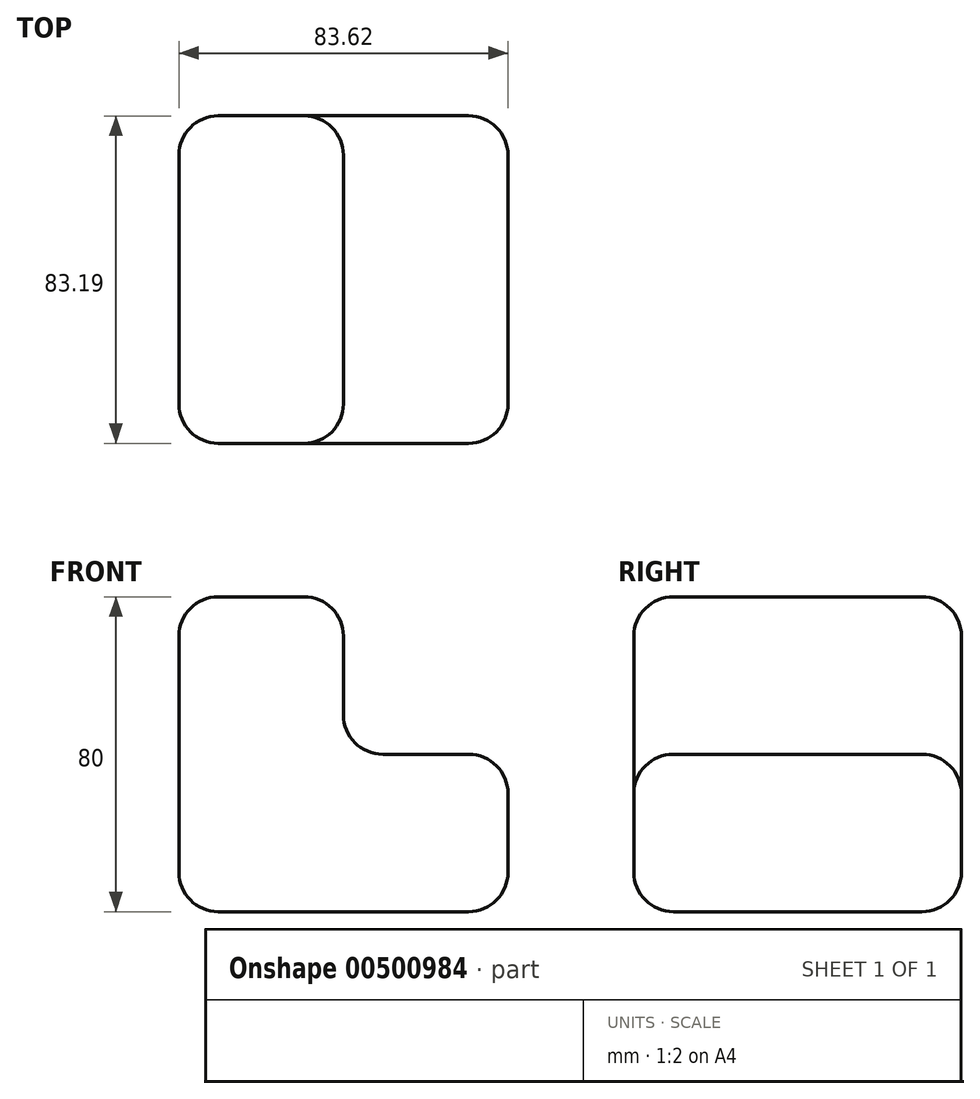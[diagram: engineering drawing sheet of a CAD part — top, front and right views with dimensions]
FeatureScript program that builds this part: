
annotation { "Feature Type Name" : "Feature", "Feature Type Description" : "" }
export const myFeature = defineFeature(function(context is Context, id is Id, definition is map)
    precondition{}
    {
        {
            var Q0;
            Q0=qCreatedBy(makeId("Top.planeOp"),FACE);
            var sketch = newSketch(context, id + "F0", { "sketchPlane" : qUnion([Q0])});
            skLineSegment(sketch, "E0.bottom", {"start": v(-59.13, -45.93) * mm, "end": v(24.5, -45.93) * mm});
            skLineSegment(sketch, "E0.top", {"start": v(-59.13, 37.26) * mm, "end": v(24.5, 37.26) * mm});
            skLineSegment(sketch, "E0.left", {"start": v(-59.13, -45.93) * mm, "end": v(-59.13, 37.26) * mm});
            skLineSegment(sketch, "E0.right", {"start": v(24.5, -45.93) * mm, "end": v(24.5, 37.26) * mm});
            skSolve(sketch);
        }
        {
            var Q0;
            Q0=makeQuery(id+"F0.imprint","IMPRINT",FACE,{"disambiguationData":[TD([[makeQuery(id+"F0.imprint","IMPRINT",EDGE,{"derivedFrom":sQuery(id+"F0.wireOp",EDGE,"E0.bottom")}),1.0]])]});
            extrude(context, id + "F1", {"entities" : qUnion([Q0]), "depth" : 40 * mm});
        }
        {
            var Q0;
            Q0=makeQuery(id+"F1.opExtrude","CAP_FACE",FACE,{"disambiguationData":[OSD([sQuery(id+"F0.wireOp",EDGE,"E0.bottom"),sQuery(id+"F0.wireOp",EDGE,"E0.top"),sQuery(id+"F0.wireOp",EDGE,"E0.left"),sQuery(id+"F0.wireOp",EDGE,"E0.right")])],"isStart":false});
            var sketch = newSketch(context, id + "F2", { "sketchPlane" : qUnion([Q0])});
            skLineSegment(sketch, "E1", {"start": v(-17.32, 37.26) * mm, "end": v(-17.32, -45.93) * mm});
            skSolve(sketch);
        }
        {
            var Q0;
            {var subQ1=sQuery(id+"F2.wireOp",EDGE,"E1");Q0=makeQuery(id+"F2.imprint","IMPRINT",FACE,{"disambiguationData":[TD([[makeQuery(id+"F2.imprint","IMPRINT",EDGE,{"derivedFrom":subQ1}),-1.0]])]});}
            extrude(context, id + "F3", {"entities" : qUnion([Q0]), "operationType" : NewBodyOperationType.ADD, "depth" : 40 * mm});
        }
        {
            var Q0;
            Q0=makeQuery(id+"F3.opExtrude","CAP_FACE",FACE,{"disambiguationData":[OSD([sQuery(id+"F0.wireOp",EDGE,"E0.bottom"),sQuery(id+"F0.wireOp",EDGE,"E0.top"),sQuery(id+"F0.wireOp",EDGE,"E0.left"),sQuery(id+"F2.wireOp",EDGE,"E1")])],"isStart":false});
            var Q1;
            Q1=makeQuery(id+"F3.opExtrude","SWEPT_FACE",FACE,{"disambiguationData":[OSD([sQuery(id+"F2.wireOp",EDGE,"E1")])]});
            var Q2;
            Q2=makeQuery(id+"F1.opExtrude","CAP_FACE",FACE,{"disambiguationData":[OSD([sQuery(id+"F0.wireOp",EDGE,"E0.bottom"),sQuery(id+"F0.wireOp",EDGE,"E0.top"),sQuery(id+"F0.wireOp",EDGE,"E0.left"),sQuery(id+"F0.wireOp",EDGE,"E0.right")])],"isStart":false});
            var Q3;
            {var subQ0=sQuery(id+"F0.wireOp",EDGE,"E0.bottom");Q3=makeQuery(id+"F3.boolean.opBoolean","MERGE",FACE,{"derivedFrom":[makeQuery(id+"F1.opExtrude","SWEPT_FACE",FACE,{"disambiguationData":[OSD([subQ0])]}),makeQuery(id+"F3.opExtrude","SWEPT_FACE",FACE,{"disambiguationData":[OSD([subQ0])]})]});}
            var Q4;
            Q4=makeQuery(id+"F1.opExtrude","SWEPT_FACE",FACE,{"disambiguationData":[OSD([sQuery(id+"F0.wireOp",EDGE,"E0.right")])]});
            var Q5;
            {var subQ0=sQuery(id+"F0.wireOp",EDGE,"E0.top");Q5=makeQuery(id+"F3.boolean.opBoolean","MERGE",FACE,{"derivedFrom":[makeQuery(id+"F1.opExtrude","SWEPT_FACE",FACE,{"disambiguationData":[OSD([subQ0])]}),makeQuery(id+"F3.opExtrude","SWEPT_FACE",FACE,{"disambiguationData":[OSD([subQ0])]})]});}
            var Q6;
            {var subQ0=sQuery(id+"F0.wireOp",EDGE,"E0.left");Q6=makeQuery(id+"F3.boolean.opBoolean","MERGE",FACE,{"derivedFrom":[makeQuery(id+"F1.opExtrude","SWEPT_FACE",FACE,{"disambiguationData":[OSD([subQ0])]}),makeQuery(id+"F3.opExtrude","SWEPT_FACE",FACE,{"disambiguationData":[OSD([subQ0])]})]});}
            fillet(context, id + "F4", {"entities" : qUnion([Q0, Q1, Q2, Q3, Q4, Q5, Q6]), "radius" : 10 * mm, "tangentPropagation" : true, "allowEdgeOverflow" : false});
        }
    });
